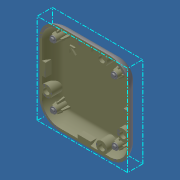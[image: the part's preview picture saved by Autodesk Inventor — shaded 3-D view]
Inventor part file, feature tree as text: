
AUTODESK INVENTOR PART (.ipt)
format: ipt  version: 2016 (Build 200138000, 138)  size: 2,255,360 bytes
history: native  units: in
note: dims shown in document units (in); Inventor stores cm internally (conversion verified against a paired STEP export)
features: other x10, plane x2, sketch x1, surface_op x1
ambient origin geometry x8: Origin, YZ Plane, XZ Plane, XY Plane, X Axis, Y Axis, Z Axis, Center Point
bodies: Solid3 (feature_tree), Solid4 (feature_tree), Solid1 (feature_tree), Solid2 (feature_tree)
feature tree (14):
  other  "Remote Bottom.ipt"
  other  "Bottom Mold_Remote Bottom_WP"
  plane  "Work Plane1"
  plane  "Work Plane2"
  other  "Cavity Separation1"
  other  "Solid1::Remote Bottom.ipt"
  other  "TaggingFeature1"
  other  "Solid1::Bottom Mold_Remote Bottom_WP"
  other  "TaggingFeature2"
  sketch  "Sketch2"  dims[d0=-0.75in d1=1.25in d2=1.25in d3=1.25in d4=1.25in d5=1.5in d6=0.0in d50=1.875in d51=1.875in d52=1.875in d53=1.875in d54=1.875in d55=1.875in d56=1.875in d57=1.875in]
  other  "Srf7"
  other  "Remote Bottom.ipt_Bodies"
  other  "Bottom Mold_Remote Bottom_WP_Bodies"
  surface_op  "Boundary Patch7"
